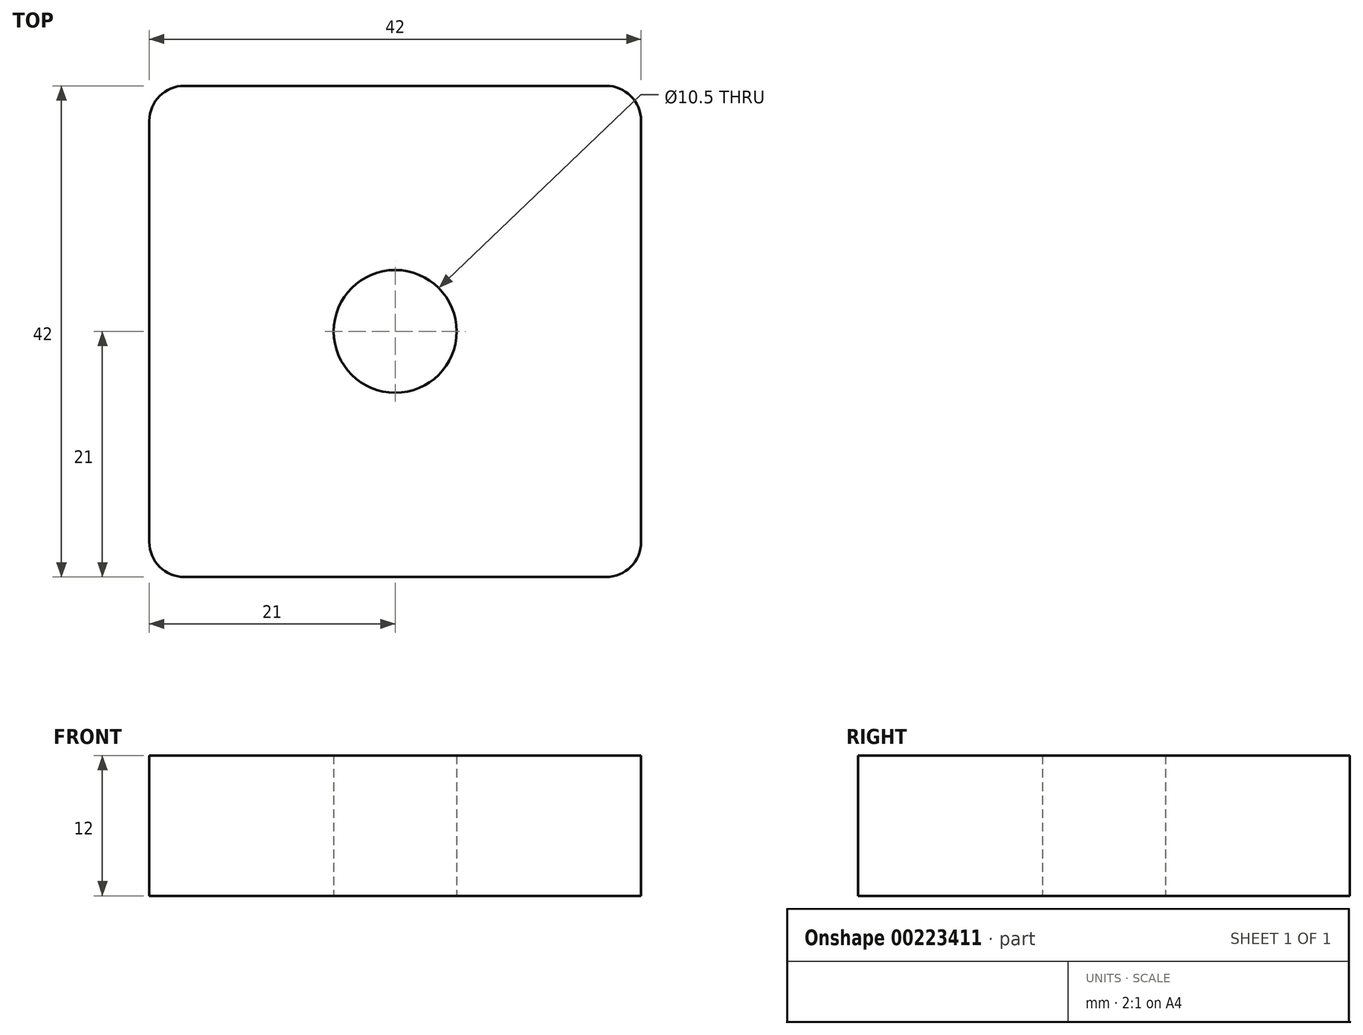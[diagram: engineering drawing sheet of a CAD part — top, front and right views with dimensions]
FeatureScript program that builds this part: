
annotation { "Feature Type Name" : "Feature", "Feature Type Description" : "" }
export const myFeature = defineFeature(function(context is Context, id is Id, definition is map)
    precondition{}
    {
        {
            var Q0;
            Q0=qCreatedBy(makeId("Top.planeOp"),FACE);
            var sketch = newSketch(context, id + "F0", { "sketchPlane" : qUnion([Q0])});
            skLineSegment(sketch, "E0.bottom", {"start": v(3, 0) * mm, "end": v(39, 0) * mm});
            skLineSegment(sketch, "E0.top", {"start": v(3, 42) * mm, "end": v(39, 42) * mm});
            skLineSegment(sketch, "E0.left", {"start": v(0, 3) * mm, "end": v(0, 39) * mm});
            skLineSegment(sketch, "E0.right", {"start": v(42, 3) * mm, "end": v(42, 39) * mm});
            skCircle(sketch, "E1", {"center": v(21, 21) * mm, "radius": 5.25 * mm});
            skPoint(sketch, "E1.centerSnap0", {"position": v(21, 0) * mm});
            skPoint(sketch, "E1.centerSnap1", {"position": v(0, 21) * mm});
            skPoint(sketch, "E2.visualSharp", {"position": v(0, 42) * mm});
            skArc(sketch, "E2.filletArc", {"start": v(3, 42) * mm, "mid": v(0.88, 41.12) * mm, "end": v(0, 39) * mm});
            skPoint(sketch, "E3.visualSharp", {"position": v(42, 42) * mm});
            skArc(sketch, "E3.filletArc", {"start": v(42, 39) * mm, "mid": v(41.12, 41.12) * mm, "end": v(39, 42) * mm});
            skPoint(sketch, "E4.visualSharp", {"position": v(42, 0) * mm});
            skArc(sketch, "E4.filletArc", {"start": v(39, 0) * mm, "mid": v(41.12, 0.88) * mm, "end": v(42, 3) * mm});
            skPoint(sketch, "E5.visualSharp", {"position": v(0, 0) * mm});
            skArc(sketch, "E5.filletArc", {"start": v(0, 3) * mm, "mid": v(0.88, 0.88) * mm, "end": v(3, 0) * mm});
            skSolve(sketch);
        }
        {
            var Q0;
            Q0=makeQuery(id+"F0.imprint","IMPRINT",FACE,{"disambiguationData":[TD([[makeQuery(id+"F0.imprint","IMPRINT",EDGE,{"derivedFrom":sQuery(id+"F0.wireOp",EDGE,"E0.bottom")}),1.0]])]});
            extrude(context, id + "F1", {"entities" : qUnion([Q0]), "depth" : 12 * mm});
        }
    });
